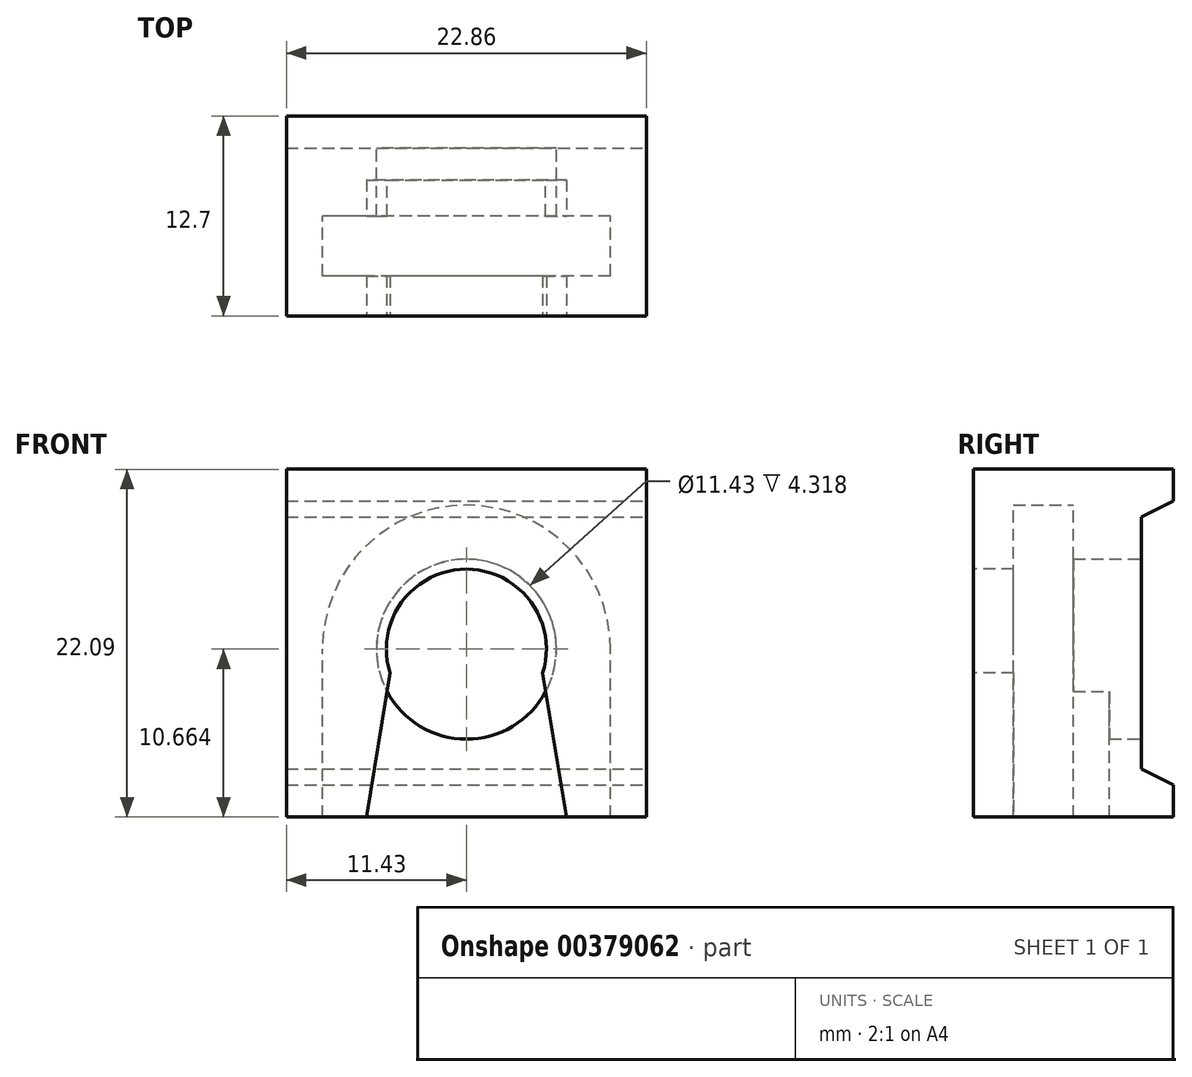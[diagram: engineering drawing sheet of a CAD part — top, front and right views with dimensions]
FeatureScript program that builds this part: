
annotation { "Feature Type Name" : "Feature", "Feature Type Description" : "" }
export const myFeature = defineFeature(function(context is Context, id is Id, definition is map)
    precondition{}
    {
        {
            var Q0;
            Q0=qCreatedBy(makeId("Front.planeOp"),FACE);
            var sketch = newSketch(context, id + "F0", { "sketchPlane" : qUnion([Q0])});
            skLineSegment(sketch, "E0.bottom", {"start": v(11.43, -5.33) * mm, "end": v(-11.43, -5.33) * mm});
            skLineSegment(sketch, "E0.left", {"start": v(11.43, -5.33) * mm, "end": v(11.43, 5.33) * mm});
            skLineSegment(sketch, "E0.right", {"start": v(-11.43, -5.33) * mm, "end": v(-11.43, 5.33) * mm});
            skPoint(sketch, "E0.middle", {"position": v(0, 0) * mm});
            skArc(sketch, "E1", {"start": v(11.43, 5.33) * mm, "mid": v(0, 16.76) * mm, "end": v(-11.43, 5.33) * mm, "construction": true});
            skPoint(sketch, "E2", {"position": v(0, 16.76) * mm});
            skLineSegment(sketch, "E3", {"start": v(-11.43, 5.33) * mm, "end": v(-11.43, 16.76) * mm});
            skLineSegment(sketch, "E4", {"start": v(-11.43, 16.76) * mm, "end": v(11.43, 16.76) * mm});
            skLineSegment(sketch, "E5", {"start": v(11.43, 16.76) * mm, "end": v(11.43, 5.33) * mm});
            skSolve(sketch);
        }
        {
            var Q0;
            Q0=qSketchRegion(id+"F0",true);
            extrude(context, id + "F1", {"entities" : qUnion([Q0]), "depth" : 12.7 * mm});
        }
        {
            var Q0;
            Q0=qCreatedBy(makeId("Front.planeOp"),FACE);
            cPlane(context, id + "F2", {"entities" : qUnion([Q0]), "cplaneType" : CPlaneType.OFFSET, "offset" : 6.35 * mm, "width" : 152.4 * mm, "height" : 152.4 * mm});
        }
        {
            var Q0;
            Q0=qCreatedBy(id+"F2.planeOp",FACE);
            var sketch = newSketch(context, id + "F3", { "sketchPlane" : qUnion([Q0])});
            skLineSegment(sketch, "E6.bottom", {"start": v(9.14, -5.33) * mm, "end": v(-9.14, -5.33) * mm});
            skLineSegment(sketch, "E6.left", {"start": v(9.14, -5.33) * mm, "end": v(9.14, 5.33) * mm});
            skLineSegment(sketch, "E6.right", {"start": v(-9.14, -5.33) * mm, "end": v(-9.14, 5.33) * mm});
            skLineSegment(sketch, "E7", {"start": v(0, -5.33) * mm, "end": v(0, 19.01) * mm, "construction": true});
            skArc(sketch, "E8", {"start": v(9.14, 5.33) * mm, "mid": v(0, 14.48) * mm, "end": v(-9.14, 5.33) * mm});
            skPoint(sketch, "E9", {"position": v(0, 14.48) * mm});
            skSolve(sketch);
        }
        {
            var Q0;
            Q0=qSketchRegion(id+"F3",true);
            extrude(context, id + "F4", {"entities" : qUnion([Q0]), "operationType" : NewBodyOperationType.REMOVE, "depth" : 3.8 * mm});
        }
        {
            var Q0;
            Q0=makeQuery(id+"F1.opExtrude","CAP_FACE",FACE,{"disambiguationData":[OSD([sQuery(id+"F0.wireOp",EDGE,"E0.bottom"),sQuery(id+"F0.wireOp",EDGE,"E0.left"),sQuery(id+"F0.wireOp",EDGE,"E0.right"),sQuery(id+"F0.wireOp",EDGE,"E1")])],"isStart":false});
            var sketch = newSketch(context, id + "F5", { "sketchPlane" : qUnion([Q0])});
            skArc(sketch, "E10", {"start": v(4.85, 3.8) * mm, "mid": v(0, 10.41) * mm, "end": v(-4.85, 3.81) * mm});
            skLineSegment(sketch, "E11", {"start": v(4.85, 3.8) * mm, "end": v(-4.85, 3.8) * mm, "construction": true});
            skLineSegment(sketch, "E12", {"start": v(4.85, 3.81) * mm, "end": v(6.35, -5.33) * mm});
            skLineSegment(sketch, "E13", {"start": v(6.35, -5.33) * mm, "end": v(-6.35, -5.33) * mm});
            skLineSegment(sketch, "E14", {"start": v(-6.35, -5.33) * mm, "end": v(-4.85, 3.81) * mm});
            skLineSegment(sketch, "E15", {"start": v(0, -5.33) * mm, "end": v(0, 5.33) * mm, "construction": true});
            skSolve(sketch);
        }
        {
            var Q0;
            Q0=qSketchRegion(id+"F5",true);
            extrude(context, id + "F6", {"entities" : qUnion([Q0]), "operationType" : NewBodyOperationType.REMOVE, "oppositeDirection" : true, "depth" : 8.64 * mm});
        }
        {
            var Q0;
            Q0=makeQuery(id+"F1.opExtrude","SWEPT_FACE",FACE,{"disambiguationData":[OSD([sQuery(id+"F0.wireOp",EDGE,"E0.left")])]});
            var sketch = newSketch(context, id + "F7", { "sketchPlane" : qUnion([Q0])});
            skLineSegment(sketch, "E16", {"start": v(0, -3.3) * mm, "end": v(-2.03, -2.29) * mm});
            skLineSegment(sketch, "E17", {"start": v(-2.03, -2.29) * mm, "end": v(-2.03, 13.72) * mm});
            skLineSegment(sketch, "E18", {"start": v(-2.03, 13.72) * mm, "end": v(0, 14.73) * mm});
            skLineSegment(sketch, "E19", {"start": v(0, 14.73) * mm, "end": v(0, -3.3) * mm});
            skLineSegment(sketch, "E20", {"start": v(-2.03, 5.71) * mm, "end": v(0, 5.71) * mm, "construction": true});
            skPoint(sketch, "E20.startSnap0", {"position": v(0, 5.71) * mm});
            skSolve(sketch);
        }
        {
            var Q0;
            Q0=qSketchRegion(id+"F7",true);
            extrude(context, id + "F8", {"entities" : qUnion([Q0]), "operationType" : NewBodyOperationType.REMOVE, "oppositeDirection" : true, "depth" : 25.4 * mm});
        }
        {
            var Q0;
            Q0=makeQuery(id+"F8.boolean.opBoolean","COPY",FACE,{"derivedFrom":makeQuery(id+"F8.opExtrude","SWEPT_FACE",FACE,{"disambiguationData":[OSD([sQuery(id+"F7.wireOp",EDGE,"E17")])]})});
            var sketch = newSketch(context, id + "F9", { "sketchPlane" : qUnion([Q0])});
            skCircle(sketch, "E21", {"center": v(0, 5.33) * mm, "radius": 5.72 * mm});
            skSolve(sketch);
        }
        {
            var Q0;
            Q0=qSketchRegion(id+"F9",true);
            var Q1;
            Q1=qCreatedBy(id+"F2.planeOp",FACE);
            extrude(context, id + "F10", {"entities" : qUnion([Q0]), "operationType" : NewBodyOperationType.REMOVE, "endBound" : BoundingType.UP_TO_SURFACE, "oppositeDirection" : true, "endBoundEntityFace" : qUnion([Q1]), "depth" : 25.4 * mm});
        }
    });
